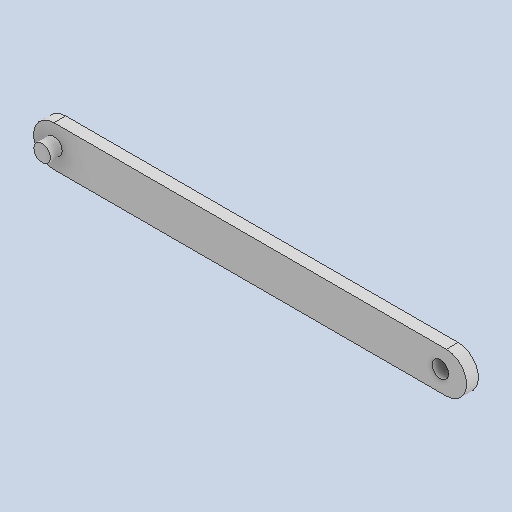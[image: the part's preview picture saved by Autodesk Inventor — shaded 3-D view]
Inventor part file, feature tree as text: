
AUTODESK INVENTOR PART (.ipt)
format: ipt  version: 2024.1 (Build 281209000, 209)  size: 253,440 bytes
history: native  units: mm
features: extrude x5, sketch x5
ambient origin geometry x8: Origin, YZ Plane, XZ Plane, XY Plane, X Axis, Y Axis, Z Axis, Center Point
bodies: Solid1 (feature_tree)
feature tree (10):
  extrude  "Extrusion1"  Depth=3.0mm TaperAngle=0.0deg
  extrude  "Extrusion2"  Depth=3.0mm TaperAngle=0.0deg
  extrude  "Extrusion3"  Depth=3.0mm TaperAngle=0.0deg
  extrude  "Extrusion4"  Depth=10.0mm TaperAngle=0.0deg
  extrude  "Extrusion5"  Depth=10.0mm TaperAngle=0.0deg
  sketch  "Sketch1"  dims[d0=100.0mm d1=3.0mm d2=0.0mm]
  sketch  "Sketch2"  dims[d3=4.25mm d4=3.0mm d5=6.0mm d6=0.0mm d7=0.0mm]
  sketch  "Sketch3"  dims[d8=4.25mm d9=3.0mm d10=0.0mm]
  sketch  "Sketch4"  dims[d11=4.25mm d12=10.0mm d13=0.0mm]
  sketch  "Sketch5"  dims[d14=4.25mm d15=10.0mm d16=0.0mm]
